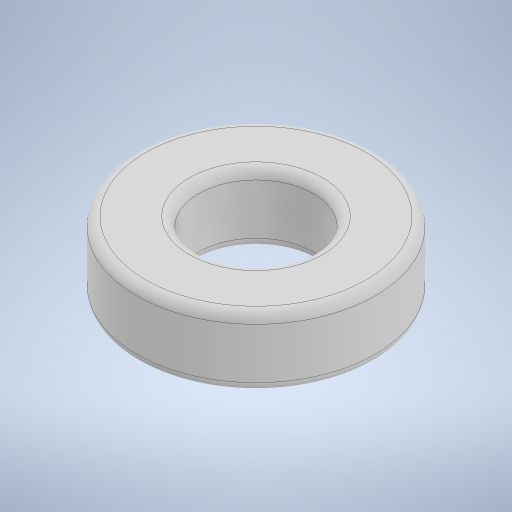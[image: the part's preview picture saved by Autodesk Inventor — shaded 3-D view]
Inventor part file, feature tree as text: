
AUTODESK INVENTOR PART (.ipt)
format: ipt  version: 2024 (Build 280153000, 153)  size: 254,976 bytes
history: native  units: mm
features: extrude x1, fillet x1, sketch x1
ambient origin geometry x8: Origin, YZ Plane, XZ Plane, XY Plane, X Axis, Y Axis, Z Axis, Center Point
bodies: Solid1 (feature_tree)
feature tree (3):
  extrude  "Extrusion1"  Depth=2.0mm
  fillet  "Fillet1"  Radius=15.0mm
  sketch  "Sketch1"  dims[d0=25.0mm d1=52.0mm d2=15.0mm d3=0.0mm d4=2.0mm]
